# Revit family: JC KONTAKTER JCK158 Armbågskontakt
name_source: partatom
category: Specialty Equipment
units: mm (PartAtom-declared; Revit-internal decimal feet)

## family parameters
Always vertical = Yes
Cut with Voids When Loaded = No
Enable Cutting in Views = Yes
Host = Wall
Maintain Annotation Orientation = No
Part Type = Normal
Room Calculation Point = No
Round Connector Dimension = Use Diameter
Shared = No

## types (2) — shared parameters
CE Dokument = https://jckontakter.se
Core Finish = Aluminum ENAW 6060
Description = Kombinerad armbågskontakt/sparkkontakt. Lång modell som är tillverkad i svarteloxerad aluminium, med tryckyta upptill och sparkyta i botten.

JCK158 tillhör en serie armbågskontakter som är kombinerade med sparkkontakt nedtill. Modellerna är särskilt utvecklade för att underlätta för t.ex. sjukhuspersonal att snabbt och enkelt kunna öppna dörrar med t.ex. sängen, armbågen, höften eller foten.
End Cap Finish = POM Tenac C 4520
Lid Finish = Aluminum ENAW 6060
Lägsta märkström = 1mA/4 V DC
Manufacturer = JC Kontakter
Mikrobrytare = Standard NO IP67
Model = JCK158
Placering av armbågskontakt = https://jckontakter.se
Tekniskt produktblad = https://jckontakter.se
Tillvalsförteckning = https://jckontakter.se
Tillverkningsland = Sverige
URL = https://jckontakter.se
zero-valued in all types: Default Elevation

## per-type parameters (varying)
| type | Antal mikrobrytare | Nominell märkström | Produktvikt |
| Type 1 | 2 | 0,1A - 10 A/250 V AC | 0.305 kg |
| Armbågskontakt JCK158 | 5 | 12 V - Resistive 6A Inductive L/R 5ms 6A, 24 V - Resistive 6A Inductive L/R 5ms 5A | 1.905 kg |

## geometry (parser evidence)
native form markers: Sweep x7
no freeform markers — native parametric forms only
